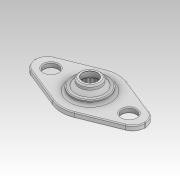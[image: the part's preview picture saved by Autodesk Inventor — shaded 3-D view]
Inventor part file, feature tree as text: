
AUTODESK INVENTOR PART (.ipt)
format: ipt  version: 2022 (Build 260153000, 153)  size: 981,504 bytes
history: native  units: mm
features: sketch x8, other x7, extrude x6, revolve x3, fillet x3, pattern_circular x1, imported_body x1
ambient origin geometry x8: Origin, YZ Plane, XZ Plane, XY Plane, X Axis, Y Axis, Z Axis, Center Point
bodies: Solid1 (feature_tree)
feature tree (29):
  other  "HD_mastersketch.ipt"
  other  "Blocks"
  revolve  "Revolution1"  [1 undecoded]
  extrude  "Extrusion1"  Depth=5.0mm
  extrude  "Extrusion2"  TaperAngle=0.0deg  [1 undecoded]
  fillet  "Fillet1"  [1 undecoded]
  extrude  "Extrusion7"  Depth=12.6mm
  extrude  "Extrusion10"  TaperAngle=0.0deg  [1 undecoded]
  pattern_circular  "Circular Pattern1"  Angle=90.0deg  [1 undecoded]
  revolve  "Revolution3"  [1 undecoded]
  fillet  "Fillet5"  Radius=0.75mm
  fillet  "Fillet6"  Radius=10.9mm
  revolve  "Revolution4"  [1 undecoded]
  extrude  "Extrusion8"  Depth=200.0mm TaperAngle=360.0deg
  extrude  "Extrusion9"  Depth=0.2mm
  other  "608 bearing"
  other  "Belt"
  other  "Rotor"
  imported_body  "Base"
  sketch  "Sketch8"  dims[d1=10.0mm d24=7.0mm d25=22.0mm d26=8.0mm]
  sketch  "Sketch9"  dims[d2=90.0deg d3=5.0mm d4=10.0mm]
  sketch  "Sketch15"  dims[d5=15.0mm d6=0.0mm d7=0.0mm d8=0.0mm d9=0.0mm]
  sketch  "Sketch16"  dims[d10=7.0mm d44=12.6mm]
  sketch  "Sketch17"  dims[d45=10.0mm d46=0.0mm d47=0.0mm d48=0.0mm]
  sketch  "Sketch18"  dims[d49=4.5mm d50=0.0mm]
  sketch  "Sketch19"  dims[d51=8.726646mm]
  sketch  "Sketch20"  dims[d52=1.0mm d53=90.0deg d54=0.5mm d55=0.75mm d56=10.9mm d58=4.5mm d59=0.0mm d60=200.0mm d61=360.0deg d63=0.2mm d68=6.0mm d69=4.1mm d70=4.2mm d72=45.0deg d73=2.0mm d74=0.75mm d75=0.75mm d76=0.1mm d77=0.1mm d78=90.0deg d79=0.8mm d80=45.0deg d81=45.0deg d82=12.6mm]
  other  "608 bearing:1"
  other  "608 bearing:2"
note: 7 required parameter values undecoded (feature->parameter linkage not recoverable at this tier; creation-order binding heuristic only, values carry confidence <= 0.55)